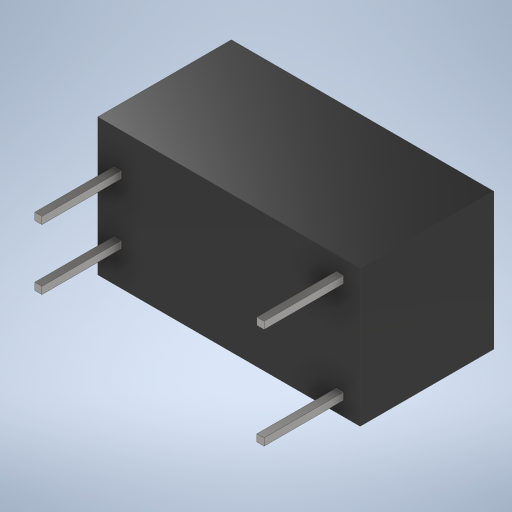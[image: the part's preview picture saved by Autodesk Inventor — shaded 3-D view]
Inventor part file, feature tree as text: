
AUTODESK INVENTOR PART (.ipt)
format: ipt  version: 2023 (Build 270158000, 158)  size: 258,560 bytes
history: native  units: mm
features: extrude x2, other x1, sketch x1
ambient origin geometry x8: Origin, YZ Plane, XZ Plane, XY Plane, X Axis, Y Axis, Z Axis, Center Point
bodies: Body1 (feature_tree)
feature tree (4):
  other  "솔리드1"
  sketch  "스케치1"
  extrude  "돌출1"  Depth=33.0mm
  extrude  "돌출2"  Depth=17.2mm
